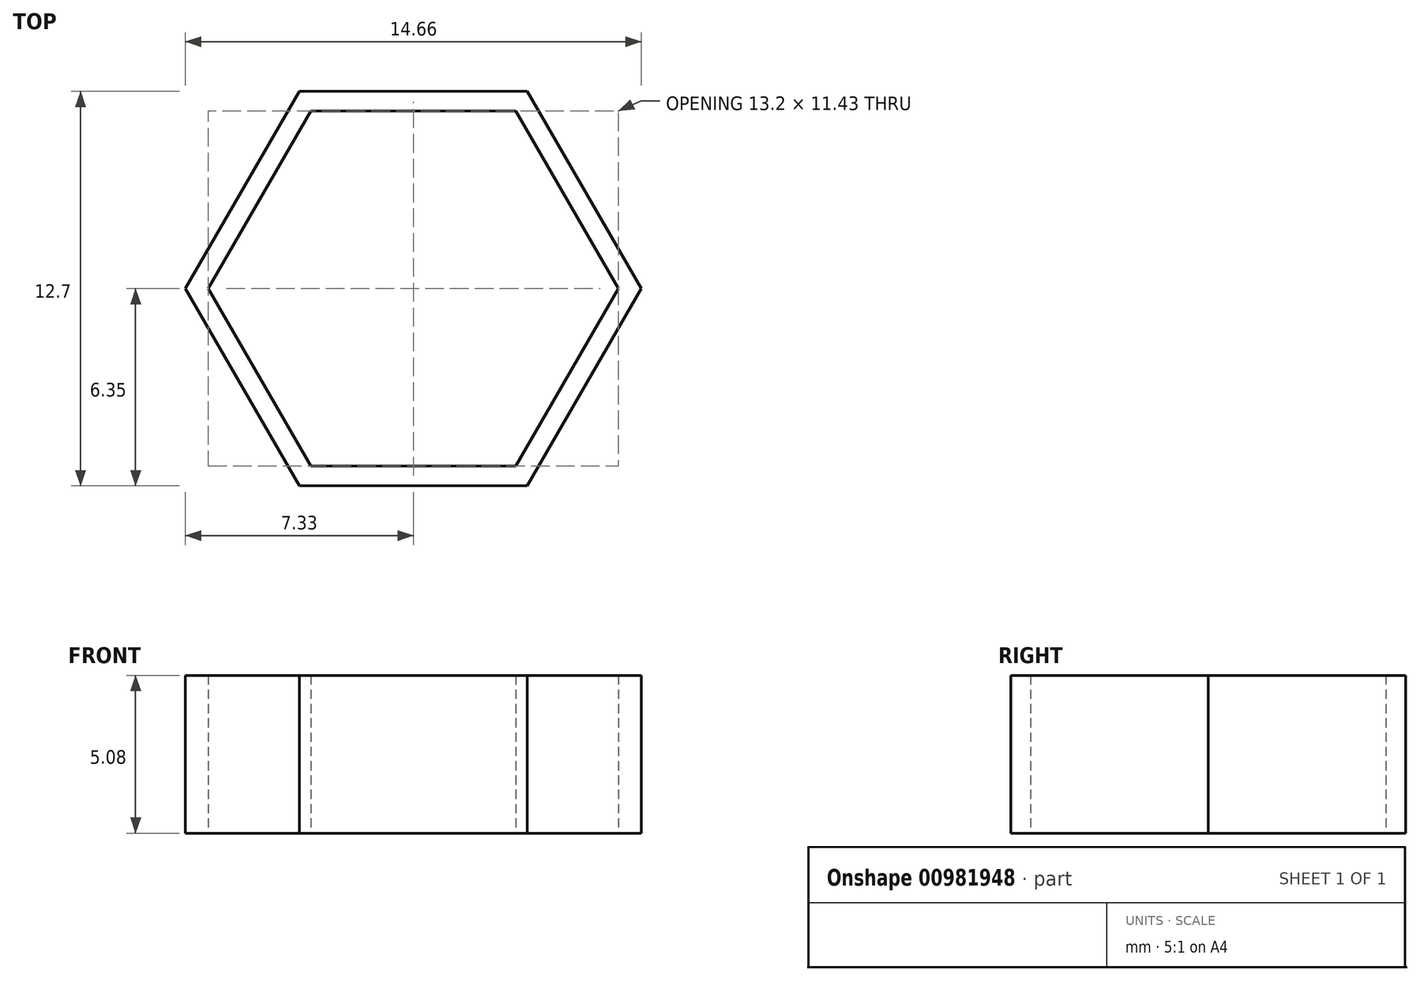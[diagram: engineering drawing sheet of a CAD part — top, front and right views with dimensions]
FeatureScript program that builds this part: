
annotation { "Feature Type Name" : "Feature", "Feature Type Description" : "" }
export const myFeature = defineFeature(function(context is Context, id is Id, definition is map)
    precondition{}
    {
        {
            var Q0;
            Q0=qCreatedBy(makeId("Top.planeOp"),FACE);
            var sketch = newSketch(context, id + "F0", { "sketchPlane" : qUnion([Q0])});
            skCircle(sketch, "E0.cCircle", {"center": v(0, 0) * mm, "radius": 5.72 * mm, "construction": true});
            skLineSegment(sketch, "E0.0", {"start": v(-3.3, 5.72) * mm, "end": v(3.3, 5.72) * mm});
            skLineSegment(sketch, "E0.1", {"start": v(3.3, 5.72) * mm, "end": v(6.6, 0) * mm});
            skLineSegment(sketch, "E0.2", {"start": v(6.6, 0) * mm, "end": v(3.3, -5.72) * mm});
            skLineSegment(sketch, "E0.3", {"start": v(3.3, -5.72) * mm, "end": v(-3.3, -5.72) * mm});
            skLineSegment(sketch, "E0.4", {"start": v(-3.3, -5.72) * mm, "end": v(-6.6, 0) * mm});
            skLineSegment(sketch, "E0.5", {"start": v(-6.6, 0) * mm, "end": v(-3.3, 5.72) * mm});
            skPoint(sketch, "E0.0.midPoint", {"position": v(0, 5.72) * mm});
            skCircle(sketch, "E1.cCircle", {"center": v(0, 0) * mm, "radius": 6.35 * mm, "construction": true});
            skLineSegment(sketch, "E1.0", {"start": v(-3.67, 6.35) * mm, "end": v(3.67, 6.35) * mm});
            skLineSegment(sketch, "E1.1", {"start": v(3.67, 6.35) * mm, "end": v(7.33, 0) * mm});
            skLineSegment(sketch, "E1.2", {"start": v(7.33, 0) * mm, "end": v(3.67, -6.35) * mm});
            skLineSegment(sketch, "E1.3", {"start": v(3.67, -6.35) * mm, "end": v(-3.67, -6.35) * mm});
            skLineSegment(sketch, "E1.4", {"start": v(-3.67, -6.35) * mm, "end": v(-7.33, 0) * mm});
            skLineSegment(sketch, "E1.5", {"start": v(-7.33, 0) * mm, "end": v(-3.67, 6.35) * mm});
            skPoint(sketch, "E1.0.midPoint", {"position": v(0, 6.35) * mm});
            skSolve(sketch);
        }
        {
            var Q0;
            Q0=qSketchRegion(id+"F0",true);
            extrude(context, id + "F1", {"entities" : qUnion([Q0]), "depth" : 5.08 * mm, "offsetDistance" : 25.4 * mm});
        }
    });
